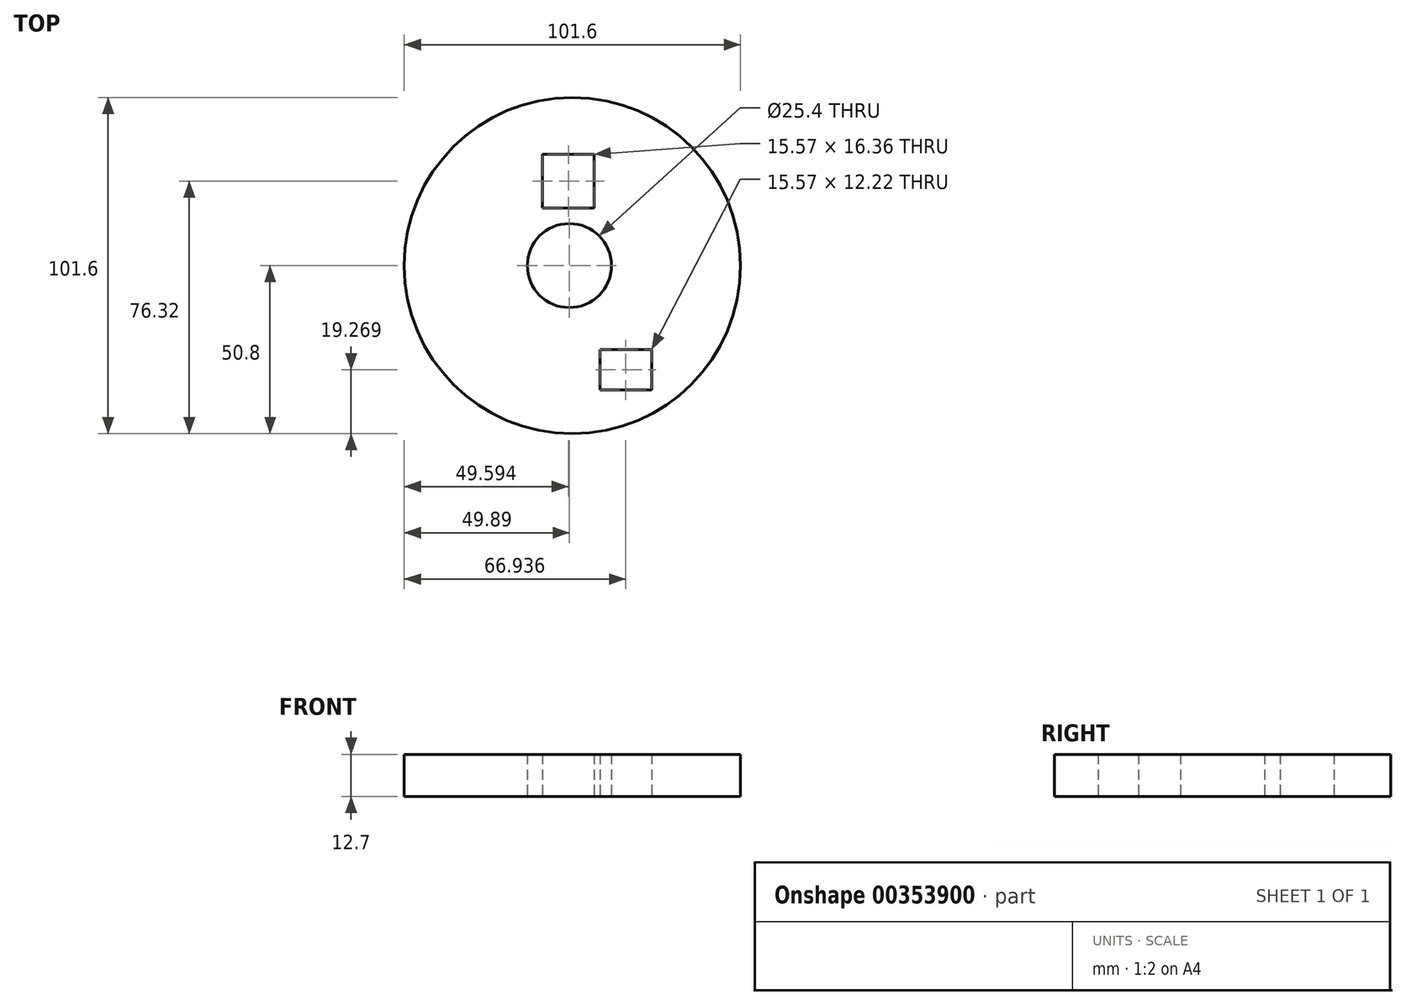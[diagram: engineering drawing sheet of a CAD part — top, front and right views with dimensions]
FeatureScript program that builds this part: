
annotation { "Feature Type Name" : "Feature", "Feature Type Description" : "" }
export const myFeature = defineFeature(function(context is Context, id is Id, definition is map)
    precondition{}
    {
        {
            var Q0;
            Q0=qCreatedBy(makeId("Top.planeOp"),FACE);
            var sketch = newSketch(context, id + "F0", { "sketchPlane" : qUnion([Q0])});
            skCircle(sketch, "E0", {"center": v(0.9, 0) * mm, "radius": 50.8 * mm});
            skCircle(sketch, "E1", {"center": v(0, 0) * mm, "radius": 12.7 * mm});
            skLineSegment(sketch, "E2.bottom", {"start": v(-8.08, 33.7) * mm, "end": v(7.49, 33.7) * mm});
            skLineSegment(sketch, "E2.top", {"start": v(-8.08, 17.34) * mm, "end": v(7.49, 17.34) * mm});
            skLineSegment(sketch, "E2.left", {"start": v(-8.08, 33.7) * mm, "end": v(-8.08, 17.34) * mm});
            skLineSegment(sketch, "E2.right", {"start": v(7.49, 33.7) * mm, "end": v(7.49, 17.34) * mm});
            skLineSegment(sketch, "E3.bottom", {"start": v(9.26, -25.42) * mm, "end": v(24.83, -25.42) * mm});
            skLineSegment(sketch, "E3.top", {"start": v(9.26, -37.64) * mm, "end": v(24.83, -37.64) * mm});
            skLineSegment(sketch, "E3.left", {"start": v(9.26, -25.42) * mm, "end": v(9.26, -37.64) * mm});
            skLineSegment(sketch, "E3.right", {"start": v(24.83, -25.42) * mm, "end": v(24.83, -37.64) * mm});
            skSolve(sketch);
        }
        {
            var Q0;
            Q0 = qSketchRegion(id + "F0", true);
            extrude(context, id + "F1", {"entities" : qUnion([Q0]), "depth" : 12.7 * mm});
        }
    });
